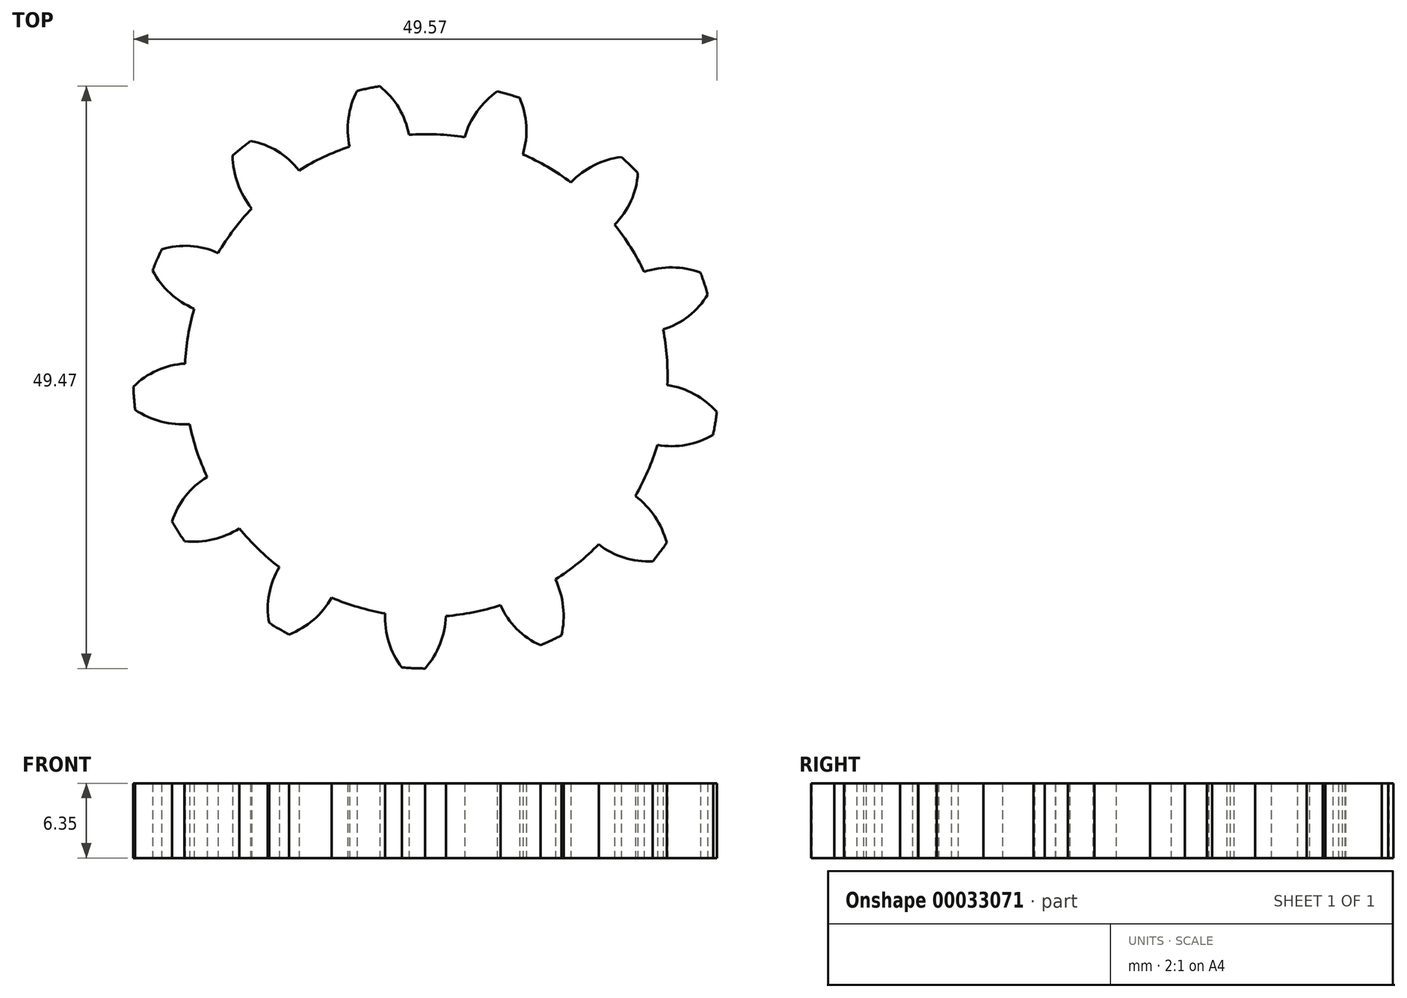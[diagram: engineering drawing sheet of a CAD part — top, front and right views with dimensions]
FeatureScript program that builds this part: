
annotation { "Feature Type Name" : "Feature", "Feature Type Description" : "" }
export const myFeature = defineFeature(function(context is Context, id is Id, definition is map)
    precondition{}
    {
        {
            var Q0;
            Q0=qCreatedBy(makeId("Top.planeOp"),FACE);
            var sketch = newSketch(context, id + "F0", { "sketchPlane" : qUnion([Q0])});
            skCircle(sketch, "E0", {"center": v(0, 0) * mm, "radius": 25.4 * mm, "construction": true});
            skCircle(sketch, "E1", {"center": v(0, 0) * mm, "radius": 24.9 * mm});
            skCircle(sketch, "E2", {"center": v(0, 0) * mm, "radius": 22.13 * mm, "construction": true});
            skCircle(sketch, "E3", {"center": v(0, 0) * mm, "radius": 20.9 * mm, "construction": true});
            skLineSegment(sketch, "E4", {"start": v(0, 20.9) * mm, "end": v(0, 25.4) * mm, "construction": true});
            skLineSegment(sketch, "E5", {"start": v(-6.36, 24.6) * mm, "end": v(-5.23, 20.23) * mm, "construction": true});
            skLineSegment(sketch, "E6", {"start": v(-5.23, 20.23) * mm, "end": v(0, 22.13) * mm, "construction": true});
            skLineSegment(sketch, "E7", {"start": v(-13.83, 20.7) * mm, "end": v(-14.11, 21.12) * mm});
            skLineSegment(sketch, "E8", {"start": v(0, 22.13) * mm, "end": v(6.63, 24.52) * mm, "construction": true});
            skLineSegment(sketch, "E9", {"start": v(10.24, 18.22) * mm, "end": v(3.9, 21.78) * mm, "construction": true});
            skCircle(sketch, "E10", {"center": v(10.24, 18.22) * mm, "radius": 7.26 * mm});
            skLineSegment(sketch, "E11", {"start": v(3.9, 21.78) * mm, "end": v(4.4, 24.5) * mm, "construction": true});
            skLineSegment(sketch, "E12", {"start": v(15.28, 19.65) * mm, "end": v(13.58, 17.47) * mm, "construction": true});
            skLineSegment(sketch, "E13", {"start": v(10.13, 22.74) * mm, "end": v(9, 20.21) * mm, "construction": true});
            skLineSegment(sketch, "E14", {"start": v(3.9, 21.78) * mm, "end": v(10.13, 22.74) * mm, "construction": true});
            skLineSegment(sketch, "E15", {"start": v(13.58, 17.47) * mm, "end": v(10.13, 22.74) * mm, "construction": true});
            skCircle(sketch, "E16", {"center": v(0, 0) * mm, "radius": 20.5 * mm});
            skLineSegment(sketch, "E17", {"start": v(5.68, 19.55) * mm, "end": v(3.26, 20.25) * mm, "construction": true});
            skLineSegment(sketch, "E18", {"start": v(9, 20.21) * mm, "end": v(8.5, 20.25) * mm});
            skLineSegment(sketch, "E19", {"start": v(8.5, 20.25) * mm, "end": v(1.77, 20.83) * mm, "construction": true});
            skCircle(sketch, "E20", {"center": v(1.77, 20.83) * mm, "radius": 6.75 * mm});
            skLineSegment(sketch, "E21", {"start": v(5.68, 19.55) * mm, "end": v(7.21, 24.82) * mm, "construction": true});
            skLineSegment(sketch, "E22", {"start": v(9, 20.21) * mm, "end": v(3.9, 21.78) * mm, "construction": true});
            skSolve(sketch);
        }
        {
            var Q0;
            {var subQ0=sQuery(id+"F0.wireOp",EDGE,"E20");var subQ3=sQuery(id+"F0.wireOp",EDGE,"E10");var subQ4=makeQuery(id+"F0.imprint","INTERSECT",VERTEX,{"disambiguationData":[OD(1.0)],"derivedFrom":[subQ3,subQ0]});Q0=makeQuery(id+"F0.imprint","IMPRINT",FACE,{"disambiguationData":[TD([[makeQuery(id+"F0.imprint","IMPRINT",EDGE,{"disambiguationData":[TD([[subQ4,-1.0]])],"derivedFrom":subQ3}),-1.0]])]});}
            var Q1;
            {var subQ0=sQuery(id+"F0.wireOp",EDGE,"E20");var subQ3=sQuery(id+"F0.wireOp",EDGE,"E10");var subQ4=makeQuery(id+"F0.imprint","INTERSECT",VERTEX,{"disambiguationData":[OD(1.0)],"derivedFrom":[subQ3,subQ0]});Q1=makeQuery(id+"F0.imprint","IMPRINT",FACE,{"disambiguationData":[TD([[makeQuery(id+"F0.imprint","IMPRINT",EDGE,{"disambiguationData":[TD([[subQ4,-1.0]])],"derivedFrom":subQ3}),1.0]])]});}
            var Q2;
            {var subQ1=sQuery(id+"F0.wireOp",EDGE,"E16");var subQ3=sQuery(id+"F0.wireOp",EDGE,"E10");var subQ5=makeQuery(id+"F0.imprint","INTERSECT",VERTEX,{"disambiguationData":[OD(0.0)],"derivedFrom":[subQ3,subQ1]});Q2=makeQuery(id+"F0.imprint","IMPRINT",FACE,{"disambiguationData":[TD([[makeQuery(id+"F0.imprint","IMPRINT",EDGE,{"disambiguationData":[TD([[subQ5,-1.0]])],"derivedFrom":subQ3}),1.0]])]});}
            var Q3;
            {var subQ1=sQuery(id+"F0.wireOp",EDGE,"E16");var subQ3=sQuery(id+"F0.wireOp",EDGE,"E10");var subQ5=makeQuery(id+"F0.imprint","INTERSECT",VERTEX,{"disambiguationData":[OD(0.0)],"derivedFrom":[subQ3,subQ1]});Q3=makeQuery(id+"F0.imprint","IMPRINT",FACE,{"disambiguationData":[TD([[makeQuery(id+"F0.imprint","IMPRINT",EDGE,{"disambiguationData":[TD([[subQ5,-1.0]])],"derivedFrom":subQ3}),-1.0]])]});}
            var Q4;
            {var subQ0=sQuery(id+"F0.wireOp",EDGE,"E20");var subQ3=makeQuery(id+"F0.imprint","IMPRINT",VERTEX,{"derivedFrom":subQ0});Q4=makeQuery(id+"F0.imprint","IMPRINT",FACE,{"disambiguationData":[TD([[makeQuery(id+"F0.imprint","IMPRINT",EDGE,{"disambiguationData":[TD([[subQ3,-1.0]])],"derivedFrom":subQ0}),1.0]])]});}
            extrude(context, id + "F1", {"entities" : qUnion([Q0, Q1, Q2, Q3, Q4]), "depth" : 6.35 * mm});
        }
        {
            var Q0;
            Q0=makeQuery(id+"F1.opExtrude","SWEPT_BODY",BODY,{"disambiguationData":[OSD([sQuery(id+"F0.wireOp",EDGE,"E1"),sQuery(id+"F0.wireOp",EDGE,"E10"),sQuery(id+"F0.wireOp",EDGE,"E16"),sQuery(id+"F0.wireOp",EDGE,"E20")])]});
            var Q1;
            Q1=makeQuery(id+"F1.opExtrude","CAP_EDGE",EDGE,{"disambiguationData":[OSD([sQuery(id+"F0.wireOp",EDGE,"E16")])],"isStart":false});
            circularPattern(context, id + "F2", {"operationType" : NewBodyOperationType.ADD, "entities" : qUnion([Q0]), "axis" : qUnion([Q1]), "angle" : 360 * degree, "instanceCount" : round(13), "equalSpace" : true});
        }
    });
